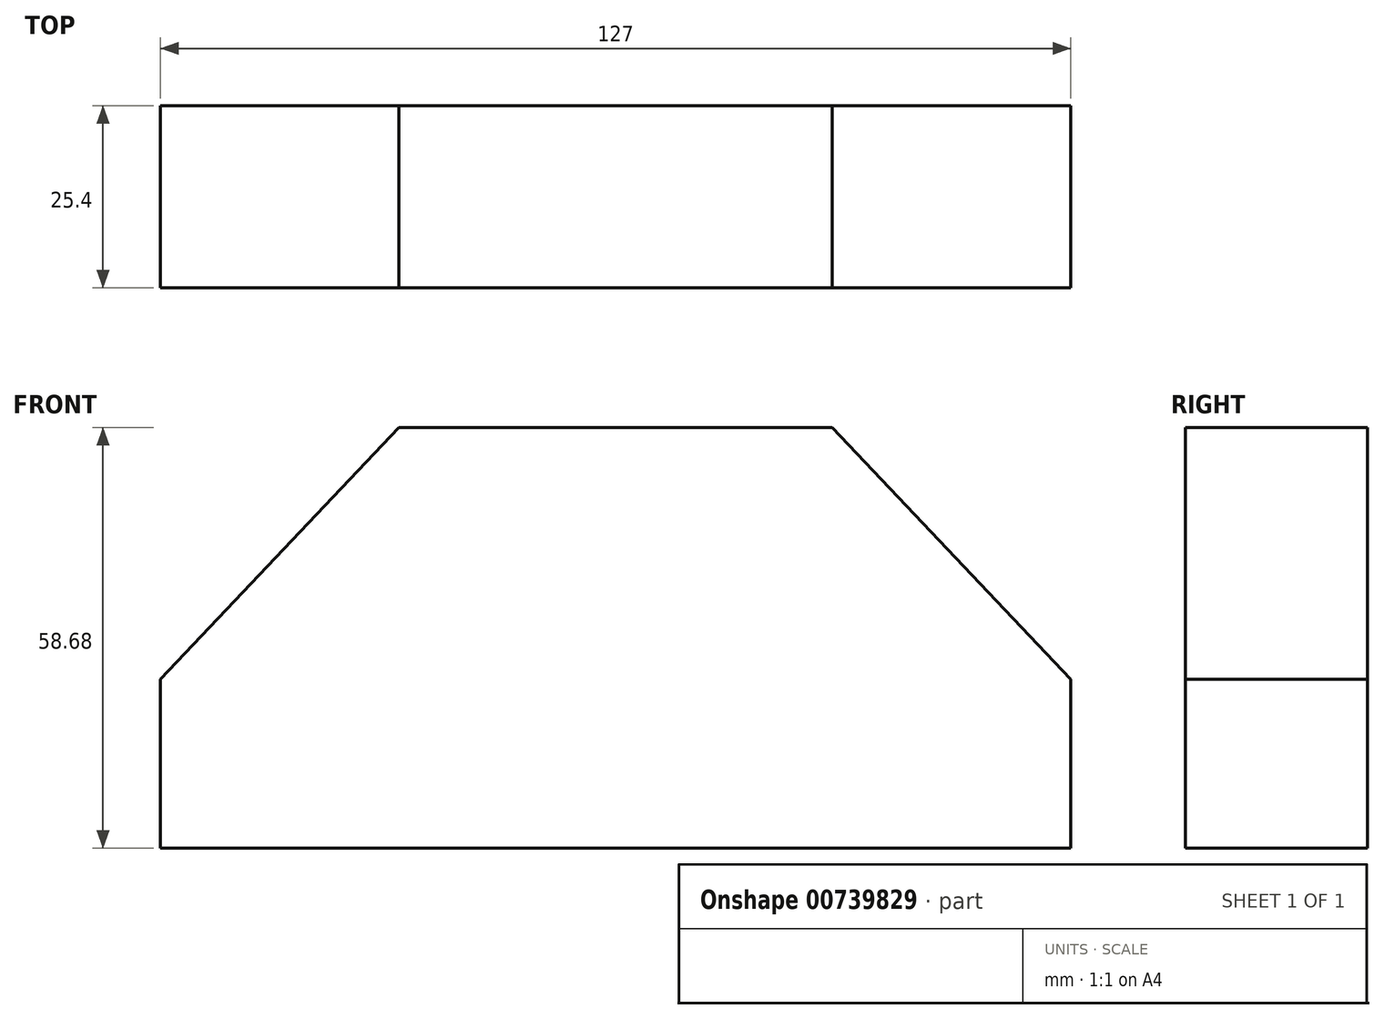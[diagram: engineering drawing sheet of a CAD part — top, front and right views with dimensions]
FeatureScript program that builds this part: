
annotation { "Feature Type Name" : "Feature", "Feature Type Description" : "" }
export const myFeature = defineFeature(function(context is Context, id is Id, definition is map)
    precondition{}
    {
        {
            var Q0;
            Q0=qCreatedBy(makeId("Front.planeOp"),FACE);
            var sketch = newSketch(context, id + "F0", { "sketchPlane" : qUnion([Q0])});
            skLineSegment(sketch, "E0", {"start": v(-64.46, -58.6) * mm, "end": v(62.54, -58.6) * mm});
            skLineSegment(sketch, "E1", {"start": v(62.54, -58.6) * mm, "end": v(62.54, -35.06) * mm});
            skLineSegment(sketch, "E2", {"start": v(62.54, -35.06) * mm, "end": v(29.27, 0.08) * mm});
            skLineSegment(sketch, "E3", {"start": v(29.27, 0.08) * mm, "end": v(-31.18, 0.08) * mm});
            skLineSegment(sketch, "E4", {"start": v(-31.18, 0.08) * mm, "end": v(-64.46, -35.06) * mm});
            skLineSegment(sketch, "E5", {"start": v(-64.46, -35.06) * mm, "end": v(-64.46, -58.6) * mm});
            skSolve(sketch);
        }
        {
            var Q0;
            Q0=makeQuery(id+"F0.imprint","IMPRINT",FACE,{"disambiguationData":[TD([[makeQuery(id+"F0.imprint","IMPRINT",EDGE,{"derivedFrom":sQuery(id+"F0.wireOp",EDGE,"E0")}),1.0]])]});
            extrude(context, id + "F1", {"entities" : qUnion([Q0]), "depth" : 25.4 * mm, "offsetDistance" : 25.4 * mm});
        }
    });
